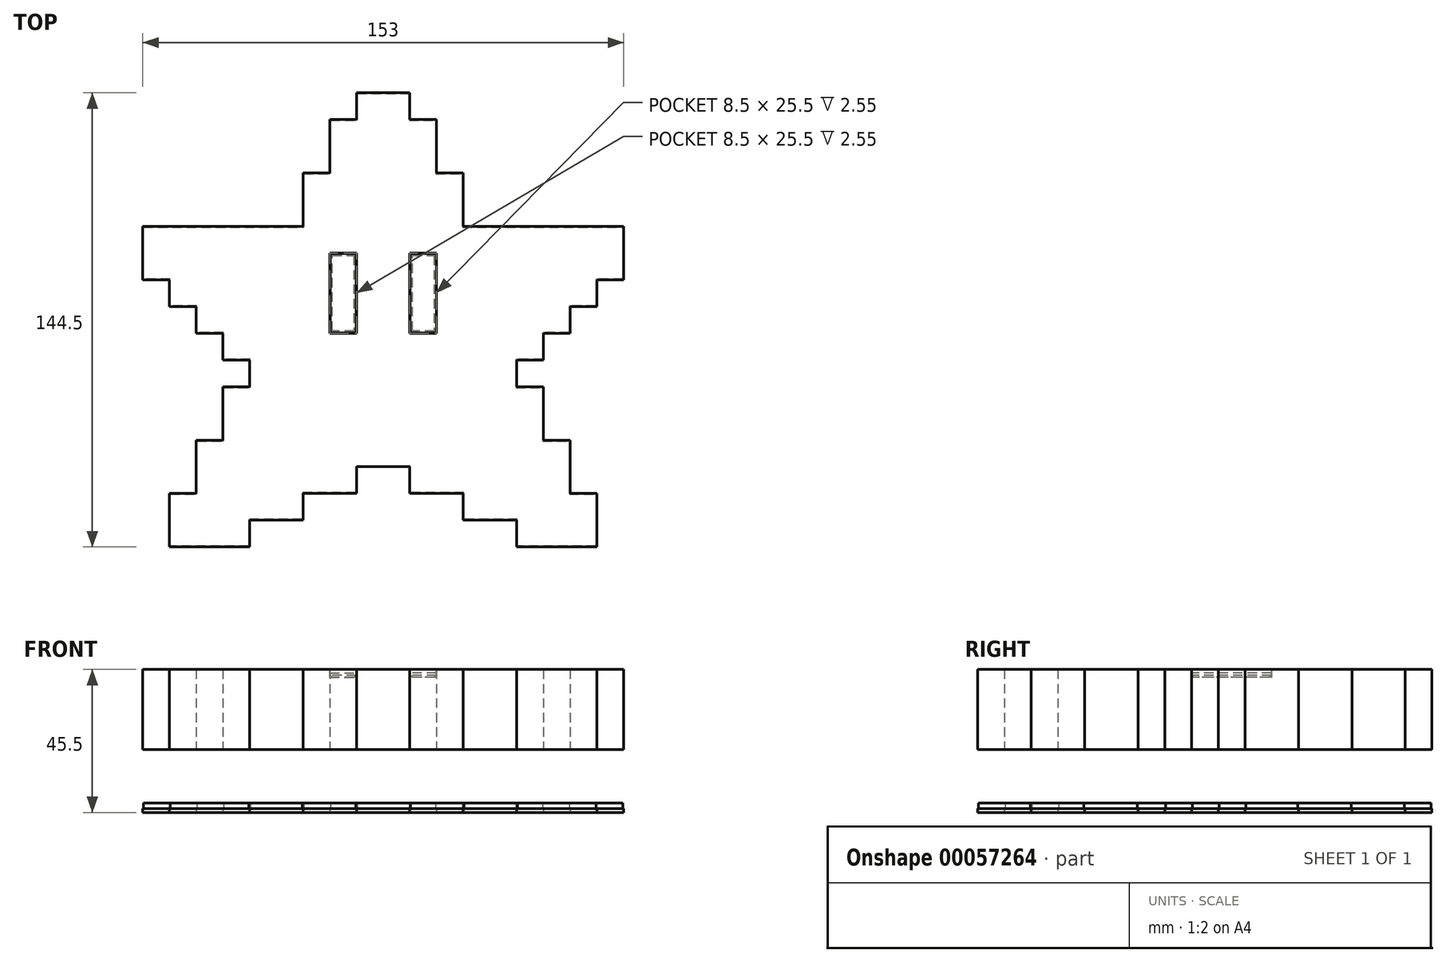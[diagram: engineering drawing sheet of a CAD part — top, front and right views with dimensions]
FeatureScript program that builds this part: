
annotation { "Feature Type Name" : "Feature", "Feature Type Description" : "" }
export const myFeature = defineFeature(function(context is Context, id is Id, definition is map)
    precondition{}
    {
        {
            assignVariable(context, id + "F0", {"name" : "pix", "anyValue" : 8.5});
        }
        {
            var Q0;
            Q0=qCreatedBy(makeId("Top.planeOp"),FACE);
            var sketch = newSketch(context, id + "F1", { "sketchPlane" : qUnion([Q0])});
            skLineSegment(sketch, "E0", {"start": v(0, 85) * mm, "end": v(-8.5, 85) * mm});
            skLineSegment(sketch, "E1", {"start": v(-8.5, 85) * mm, "end": v(-8.5, 76.5) * mm});
            skLineSegment(sketch, "E2", {"start": v(-8.5, 76.5) * mm, "end": v(-17, 76.5) * mm});
            skLineSegment(sketch, "E3", {"start": v(-17, 76.5) * mm, "end": v(-17, 59.5) * mm});
            skLineSegment(sketch, "E4", {"start": v(-17, 59.5) * mm, "end": v(-25.5, 59.5) * mm});
            skLineSegment(sketch, "E5", {"start": v(-25.5, 59.5) * mm, "end": v(-25.5, 42.5) * mm});
            skLineSegment(sketch, "E6", {"start": v(-25.5, 42.5) * mm, "end": v(-76.5, 42.5) * mm});
            skLineSegment(sketch, "E7", {"start": v(-76.5, 42.5) * mm, "end": v(-76.5, 25.5) * mm});
            skLineSegment(sketch, "E8", {"start": v(-76.5, 25.5) * mm, "end": v(-68, 25.5) * mm});
            skLineSegment(sketch, "E9", {"start": v(-68, 25.5) * mm, "end": v(-68, 17) * mm});
            skLineSegment(sketch, "E10", {"start": v(-68, 17) * mm, "end": v(-59.5, 17) * mm});
            skLineSegment(sketch, "E11", {"start": v(-59.5, 17) * mm, "end": v(-59.5, 8.5) * mm});
            skLineSegment(sketch, "E12", {"start": v(-59.5, 8.5) * mm, "end": v(-51, 8.5) * mm});
            skLineSegment(sketch, "E13", {"start": v(-51, 8.5) * mm, "end": v(-51, 0) * mm});
            skLineSegment(sketch, "E14", {"start": v(-51, 0) * mm, "end": v(-42.5, 0) * mm});
            skLineSegment(sketch, "E15", {"start": v(-42.5, 0) * mm, "end": v(-42.5, -8.5) * mm});
            skLineSegment(sketch, "E16", {"start": v(-42.5, -8.5) * mm, "end": v(-51, -8.5) * mm});
            skLineSegment(sketch, "E17", {"start": v(-51, -8.5) * mm, "end": v(-51, -25.5) * mm});
            skLineSegment(sketch, "E18", {"start": v(-51, -25.5) * mm, "end": v(-59.5, -25.5) * mm});
            skLineSegment(sketch, "E19", {"start": v(-59.5, -25.5) * mm, "end": v(-59.5, -42.5) * mm});
            skLineSegment(sketch, "E20", {"start": v(-59.5, -42.5) * mm, "end": v(-68, -42.5) * mm});
            skLineSegment(sketch, "E21", {"start": v(-68, -42.5) * mm, "end": v(-68, -59.5) * mm});
            skLineSegment(sketch, "E22", {"start": v(-68, -59.5) * mm, "end": v(-42.5, -59.5) * mm});
            skLineSegment(sketch, "E23", {"start": v(-42.5, -59.5) * mm, "end": v(-42.5, -51) * mm});
            skLineSegment(sketch, "E24", {"start": v(-42.5, -51) * mm, "end": v(-25.5, -51) * mm});
            skLineSegment(sketch, "E25", {"start": v(-25.5, -51) * mm, "end": v(-25.5, -42.5) * mm});
            skLineSegment(sketch, "E26", {"start": v(-25.5, -42.5) * mm, "end": v(-8.5, -42.5) * mm});
            skLineSegment(sketch, "E27", {"start": v(-8.5, -42.5) * mm, "end": v(-8.5, -34) * mm});
            skLineSegment(sketch, "E28", {"start": v(-8.5, -34) * mm, "end": v(0, -34) * mm});
            skLineSegment(sketch, "E29.MirrorCS", {"start": v(42.5, -8.5) * mm, "end": v(51, -8.5) * mm});
            skLineSegment(sketch, "E30.MirrorCS", {"start": v(51, -25.5) * mm, "end": v(59.5, -25.5) * mm});
            skLineSegment(sketch, "E31.MirrorCS", {"start": v(25.5, 59.5) * mm, "end": v(25.5, 42.5) * mm});
            skLineSegment(sketch, "E32.MirrorCS", {"start": v(17, 59.5) * mm, "end": v(25.5, 59.5) * mm});
            skLineSegment(sketch, "E33.MirrorCS", {"start": v(25.5, 42.5) * mm, "end": v(76.5, 42.5) * mm});
            skLineSegment(sketch, "E34.MirrorCS", {"start": v(68, -59.5) * mm, "end": v(42.5, -59.5) * mm});
            skLineSegment(sketch, "E35.MirrorCS", {"start": v(59.5, -42.5) * mm, "end": v(68, -42.5) * mm});
            skLineSegment(sketch, "E36.MirrorCS", {"start": v(76.5, 42.5) * mm, "end": v(76.5, 25.5) * mm});
            skLineSegment(sketch, "E37.MirrorCS", {"start": v(42.5, -59.5) * mm, "end": v(42.5, -51) * mm});
            skLineSegment(sketch, "E38.MirrorCS", {"start": v(17, 76.5) * mm, "end": v(17, 59.5) * mm});
            skLineSegment(sketch, "E39.MirrorCS", {"start": v(76.5, 25.5) * mm, "end": v(68, 25.5) * mm});
            skLineSegment(sketch, "E40.MirrorCS", {"start": v(8.5, 76.5) * mm, "end": v(17, 76.5) * mm});
            skLineSegment(sketch, "E41.MirrorCS", {"start": v(8.5, -34) * mm, "end": v(0, -34) * mm});
            skLineSegment(sketch, "E42.MirrorCS", {"start": v(25.5, -42.5) * mm, "end": v(8.5, -42.5) * mm});
            skLineSegment(sketch, "E43.MirrorCS", {"start": v(68, 17) * mm, "end": v(59.5, 17) * mm});
            skLineSegment(sketch, "E44.MirrorCS", {"start": v(68, 25.5) * mm, "end": v(68, 17) * mm});
            skLineSegment(sketch, "E45.MirrorCS", {"start": v(25.5, -51) * mm, "end": v(25.5, -42.5) * mm});
            skLineSegment(sketch, "E46.MirrorCS", {"start": v(8.5, -42.5) * mm, "end": v(8.5, -34) * mm});
            skLineSegment(sketch, "E47.MirrorCS", {"start": v(42.5, -51) * mm, "end": v(25.5, -51) * mm});
            skLineSegment(sketch, "E48.MirrorCS", {"start": v(8.5, 85) * mm, "end": v(8.5, 76.5) * mm});
            skLineSegment(sketch, "E49.MirrorCS", {"start": v(68, -42.5) * mm, "end": v(68, -59.5) * mm});
            skLineSegment(sketch, "E50.MirrorCS", {"start": v(0, 85) * mm, "end": v(8.5, 85) * mm});
            skLineSegment(sketch, "E51.MirrorCS", {"start": v(59.5, 8.5) * mm, "end": v(51, 8.5) * mm});
            skLineSegment(sketch, "E52.MirrorCS", {"start": v(51, 0) * mm, "end": v(42.5, 0) * mm});
            skLineSegment(sketch, "E53.MirrorCS", {"start": v(59.5, -25.5) * mm, "end": v(59.5, -42.5) * mm});
            skLineSegment(sketch, "E54.MirrorCS", {"start": v(51, 8.5) * mm, "end": v(51, 0) * mm});
            skLineSegment(sketch, "E55.MirrorCS", {"start": v(59.5, 17) * mm, "end": v(59.5, 8.5) * mm});
            skLineSegment(sketch, "E56.MirrorCS", {"start": v(51, -8.5) * mm, "end": v(51, -25.5) * mm});
            skLineSegment(sketch, "E57.MirrorCS", {"start": v(42.5, 0) * mm, "end": v(42.5, -8.5) * mm});
            skSolve(sketch);
        }
        {
            var Q0;
            Q0=makeQuery(id+"F1.imprint","IMPRINT",FACE,{"disambiguationData":[TD([[makeQuery(id+"F1.imprint","IMPRINT",EDGE,{"derivedFrom":sQuery(id+"F1.wireOp",EDGE,"E0")}),1.0]])]});
            extrude(context, id + "F2", {"entities" : qUnion([Q0]), "depth" : (3 * getVariable(context, 'pix')) * mm});
        }
        {
            var Q0;
            Q0=makeQuery(id+"F2.opExtrude","CAP_FACE",FACE,{"disambiguationData":[OSD([sQuery(id+"F1.wireOp",EDGE,"E0"),sQuery(id+"F1.wireOp",EDGE,"E1"),sQuery(id+"F1.wireOp",EDGE,"E2"),sQuery(id+"F1.wireOp",EDGE,"E3"),sQuery(id+"F1.wireOp",EDGE,"E4"),sQuery(id+"F1.wireOp",EDGE,"E5"),sQuery(id+"F1.wireOp",EDGE,"E6"),sQuery(id+"F1.wireOp",EDGE,"E7"),sQuery(id+"F1.wireOp",EDGE,"E8"),sQuery(id+"F1.wireOp",EDGE,"E9"),sQuery(id+"F1.wireOp",EDGE,"E10"),sQuery(id+"F1.wireOp",EDGE,"E11"),sQuery(id+"F1.wireOp",EDGE,"E12"),sQuery(id+"F1.wireOp",EDGE,"E13"),sQuery(id+"F1.wireOp",EDGE,"E14"),sQuery(id+"F1.wireOp",EDGE,"E15"),sQuery(id+"F1.wireOp",EDGE,"E16"),sQuery(id+"F1.wireOp",EDGE,"E17"),sQuery(id+"F1.wireOp",EDGE,"E18"),sQuery(id+"F1.wireOp",EDGE,"E19"),sQuery(id+"F1.wireOp",EDGE,"E20"),sQuery(id+"F1.wireOp",EDGE,"E21"),sQuery(id+"F1.wireOp",EDGE,"E22"),sQuery(id+"F1.wireOp",EDGE,"E23"),sQuery(id+"F1.wireOp",EDGE,"E24"),sQuery(id+"F1.wireOp",EDGE,"E25"),sQuery(id+"F1.wireOp",EDGE,"E26"),sQuery(id+"F1.wireOp",EDGE,"E27"),sQuery(id+"F1.wireOp",EDGE,"E28"),sQuery(id+"F1.wireOp",EDGE,"E29.MirrorCS"),sQuery(id+"F1.wireOp",EDGE,"E30.MirrorCS"),sQuery(id+"F1.wireOp",EDGE,"E31.MirrorCS"),sQuery(id+"F1.wireOp",EDGE,"E32.MirrorCS"),sQuery(id+"F1.wireOp",EDGE,"E33.MirrorCS"),sQuery(id+"F1.wireOp",EDGE,"E34.MirrorCS"),sQuery(id+"F1.wireOp",EDGE,"E35.MirrorCS"),sQuery(id+"F1.wireOp",EDGE,"E36.MirrorCS"),sQuery(id+"F1.wireOp",EDGE,"E37.MirrorCS"),sQuery(id+"F1.wireOp",EDGE,"E38.MirrorCS"),sQuery(id+"F1.wireOp",EDGE,"E39.MirrorCS"),sQuery(id+"F1.wireOp",EDGE,"E40.MirrorCS"),sQuery(id+"F1.wireOp",EDGE,"E41.MirrorCS"),sQuery(id+"F1.wireOp",EDGE,"E42.MirrorCS"),sQuery(id+"F1.wireOp",EDGE,"E43.MirrorCS"),sQuery(id+"F1.wireOp",EDGE,"E44.MirrorCS"),sQuery(id+"F1.wireOp",EDGE,"E45.MirrorCS"),sQuery(id+"F1.wireOp",EDGE,"E46.MirrorCS"),sQuery(id+"F1.wireOp",EDGE,"E47.MirrorCS"),sQuery(id+"F1.wireOp",EDGE,"E48.MirrorCS"),sQuery(id+"F1.wireOp",EDGE,"E49.MirrorCS"),sQuery(id+"F1.wireOp",EDGE,"E50.MirrorCS"),sQuery(id+"F1.wireOp",EDGE,"E51.MirrorCS"),sQuery(id+"F1.wireOp",EDGE,"E52.MirrorCS"),sQuery(id+"F1.wireOp",EDGE,"E53.MirrorCS"),sQuery(id+"F1.wireOp",EDGE,"E54.MirrorCS"),sQuery(id+"F1.wireOp",EDGE,"E55.MirrorCS"),sQuery(id+"F1.wireOp",EDGE,"E56.MirrorCS"),sQuery(id+"F1.wireOp",EDGE,"E57.MirrorCS")])],"isStart":false});
            var sketch = newSketch(context, id + "F3", { "sketchPlane" : qUnion([Q0])});
            skPoint(sketch, "E58.0", {"position": v(-17, 59.5) * mm});
            skLineSegment(sketch, "E59.bottom", {"start": v(-17, 34) * mm, "end": v(-8.5, 34) * mm});
            skLineSegment(sketch, "E59.top", {"start": v(-17, 8.5) * mm, "end": v(-8.5, 8.5) * mm});
            skLineSegment(sketch, "E59.left", {"start": v(-17, 34) * mm, "end": v(-17, 8.5) * mm});
            skLineSegment(sketch, "E59.right", {"start": v(-8.5, 34) * mm, "end": v(-8.5, 8.5) * mm});
            skLineSegment(sketch, "E60.MirrorCS", {"start": v(8.5, 34) * mm, "end": v(8.5, 8.5) * mm});
            skLineSegment(sketch, "E61.MirrorCS", {"start": v(17, 34) * mm, "end": v(17, 8.5) * mm});
            skLineSegment(sketch, "E62.MirrorCS", {"start": v(17, 8.5) * mm, "end": v(8.5, 8.5) * mm});
            skLineSegment(sketch, "E63.MirrorCS", {"start": v(17, 34) * mm, "end": v(8.5, 34) * mm});
            skPoint(sketch, "E64.MirrorP", {"position": v(17, 59.5) * mm});
            skSolve(sketch);
        }
        {
            var Q0;
            Q0=makeQuery(id+"F3.imprint","IMPRINT",FACE,{"disambiguationData":[TD([[makeQuery(id+"F3.imprint","IMPRINT",EDGE,{"derivedFrom":sQuery(id+"F3.wireOp",EDGE,"E59.bottom")}),-1.0]])]});
            var Q1;
            Q1=makeQuery(id+"F3.imprint","IMPRINT",FACE,{"disambiguationData":[TD([[makeQuery(id+"F3.imprint","IMPRINT",EDGE,{"derivedFrom":sQuery(id+"F3.wireOp",EDGE,"E60.MirrorCS")}),1.0]])]});
            extrude(context, id + "F4", {"entities" : qUnion([Q0, Q1]), "operationType" : NewBodyOperationType.REMOVE, "oppositeDirection" : true, "depth" : 0.3 * (getVariable(context, 'pix')) * mm});
        }
        {
            var Q0;
            Q0=makeQuery(id+"F2.opExtrude","CAP_FACE",FACE,{"disambiguationData":[OSD([sQuery(id+"F1.wireOp",EDGE,"E0"),sQuery(id+"F1.wireOp",EDGE,"E1"),sQuery(id+"F1.wireOp",EDGE,"E2"),sQuery(id+"F1.wireOp",EDGE,"E3"),sQuery(id+"F1.wireOp",EDGE,"E4"),sQuery(id+"F1.wireOp",EDGE,"E5"),sQuery(id+"F1.wireOp",EDGE,"E6"),sQuery(id+"F1.wireOp",EDGE,"E7"),sQuery(id+"F1.wireOp",EDGE,"E8"),sQuery(id+"F1.wireOp",EDGE,"E9"),sQuery(id+"F1.wireOp",EDGE,"E10"),sQuery(id+"F1.wireOp",EDGE,"E11"),sQuery(id+"F1.wireOp",EDGE,"E12"),sQuery(id+"F1.wireOp",EDGE,"E13"),sQuery(id+"F1.wireOp",EDGE,"E14"),sQuery(id+"F1.wireOp",EDGE,"E15"),sQuery(id+"F1.wireOp",EDGE,"E16"),sQuery(id+"F1.wireOp",EDGE,"E17"),sQuery(id+"F1.wireOp",EDGE,"E18"),sQuery(id+"F1.wireOp",EDGE,"E19"),sQuery(id+"F1.wireOp",EDGE,"E20"),sQuery(id+"F1.wireOp",EDGE,"E21"),sQuery(id+"F1.wireOp",EDGE,"E22"),sQuery(id+"F1.wireOp",EDGE,"E23"),sQuery(id+"F1.wireOp",EDGE,"E24"),sQuery(id+"F1.wireOp",EDGE,"E25"),sQuery(id+"F1.wireOp",EDGE,"E26"),sQuery(id+"F1.wireOp",EDGE,"E27"),sQuery(id+"F1.wireOp",EDGE,"E28"),sQuery(id+"F1.wireOp",EDGE,"E29.MirrorCS"),sQuery(id+"F1.wireOp",EDGE,"E30.MirrorCS"),sQuery(id+"F1.wireOp",EDGE,"E31.MirrorCS"),sQuery(id+"F1.wireOp",EDGE,"E32.MirrorCS"),sQuery(id+"F1.wireOp",EDGE,"E33.MirrorCS"),sQuery(id+"F1.wireOp",EDGE,"E34.MirrorCS"),sQuery(id+"F1.wireOp",EDGE,"E35.MirrorCS"),sQuery(id+"F1.wireOp",EDGE,"E36.MirrorCS"),sQuery(id+"F1.wireOp",EDGE,"E37.MirrorCS"),sQuery(id+"F1.wireOp",EDGE,"E38.MirrorCS"),sQuery(id+"F1.wireOp",EDGE,"E39.MirrorCS"),sQuery(id+"F1.wireOp",EDGE,"E40.MirrorCS"),sQuery(id+"F1.wireOp",EDGE,"E41.MirrorCS"),sQuery(id+"F1.wireOp",EDGE,"E42.MirrorCS"),sQuery(id+"F1.wireOp",EDGE,"E43.MirrorCS"),sQuery(id+"F1.wireOp",EDGE,"E44.MirrorCS"),sQuery(id+"F1.wireOp",EDGE,"E45.MirrorCS"),sQuery(id+"F1.wireOp",EDGE,"E46.MirrorCS"),sQuery(id+"F1.wireOp",EDGE,"E47.MirrorCS"),sQuery(id+"F1.wireOp",EDGE,"E48.MirrorCS"),sQuery(id+"F1.wireOp",EDGE,"E49.MirrorCS"),sQuery(id+"F1.wireOp",EDGE,"E50.MirrorCS"),sQuery(id+"F1.wireOp",EDGE,"E51.MirrorCS"),sQuery(id+"F1.wireOp",EDGE,"E52.MirrorCS"),sQuery(id+"F1.wireOp",EDGE,"E53.MirrorCS"),sQuery(id+"F1.wireOp",EDGE,"E54.MirrorCS"),sQuery(id+"F1.wireOp",EDGE,"E55.MirrorCS"),sQuery(id+"F1.wireOp",EDGE,"E56.MirrorCS"),sQuery(id+"F1.wireOp",EDGE,"E57.MirrorCS")])],"isStart":false});
            var sketch = newSketch(context, id + "F5", { "sketchPlane" : qUnion([Q0])});
            skPoint(sketch, "E65", {"position": v(0, 76.5) * mm});
            skLineSegment(sketch, "E66.rect.bottom", {"start": v(-2.13, 76.5) * mm, "end": v(2.12, 76.5) * mm});
            skLineSegment(sketch, "E66.rect.top", {"start": v(-2.13, 72.25) * mm, "end": v(2.12, 72.25) * mm});
            skLineSegment(sketch, "E66.rect.left", {"start": v(-2.13, 76.5) * mm, "end": v(-2.13, 72.25) * mm});
            skLineSegment(sketch, "E66.rect.right", {"start": v(2.12, 76.5) * mm, "end": v(2.12, 72.25) * mm});
            skPoint(sketch, "E66.rect.middle", {"position": v(0, 74.38) * mm});
            skSolve(sketch);
        }
        {
            var Q0;
            Q0=makeQuery(id+"F4.boolean.opBoolean","COPY",FACE,{"derivedFrom":makeQuery(id+"F4.opExtrude","CAP_FACE",FACE,{"disambiguationData":[OSD([sQuery(id+"F3.wireOp",EDGE,"E59.bottom"),sQuery(id+"F3.wireOp",EDGE,"E59.top"),sQuery(id+"F3.wireOp",EDGE,"E59.left"),sQuery(id+"F3.wireOp",EDGE,"E59.right")])],"isStart":false})});
            var sketch = newSketch(context, id + "F6", { "sketchPlane" : qUnion([Q0])});
            skLineSegment(sketch, "E67.0", {"start": v(-16.9, 33.9) * mm, "end": v(-8.6, 33.9) * mm});
            skLineSegment(sketch, "E67.1", {"start": v(-16.9, 33.9) * mm, "end": v(-16.9, 8.6) * mm});
            skLineSegment(sketch, "E67.2", {"start": v(-16.9, 8.6) * mm, "end": v(-8.6, 8.6) * mm});
            skLineSegment(sketch, "E67.3", {"start": v(-8.6, 33.9) * mm, "end": v(-8.6, 8.6) * mm});
            skLineSegment(sketch, "E68.MirrorCS", {"start": v(16.9, 33.9) * mm, "end": v(8.6, 33.9) * mm});
            skLineSegment(sketch, "E69.MirrorCS", {"start": v(16.9, 8.6) * mm, "end": v(8.6, 8.6) * mm});
            skLineSegment(sketch, "E70.MirrorCS", {"start": v(8.6, 33.9) * mm, "end": v(8.6, 8.6) * mm});
            skLineSegment(sketch, "E71.MirrorCS", {"start": v(16.9, 33.9) * mm, "end": v(16.9, 8.6) * mm});
            skSolve(sketch);
        }
        {
            var Q0;
            Q0=makeQuery(id+"F6.imprint","IMPRINT",FACE,{"disambiguationData":[TD([[makeQuery(id+"F6.imprint","IMPRINT",EDGE,{"derivedFrom":sQuery(id+"F6.wireOp",EDGE,"E67.0")}),-1.0]])]});
            var Q1;
            Q1=makeQuery(id+"F6.imprint","IMPRINT",FACE,{"disambiguationData":[TD([[makeQuery(id+"F6.imprint","IMPRINT",EDGE,{"derivedFrom":sQuery(id+"F6.wireOp",EDGE,"E68.MirrorCS")}),1.0]])]});
            extrude(context, id + "F7", {"entities" : qUnion([Q0, Q1]), "depth" : 1.5 * mm});
        }
        {
            var Q0;
            Q0=makeQuery(id+"F7.opExtrude","CAP_FACE",FACE,{"disambiguationData":[OSD([sQuery(id+"F6.wireOp",EDGE,"E67.0"),sQuery(id+"F6.wireOp",EDGE,"E67.1"),sQuery(id+"F6.wireOp",EDGE,"E67.2"),sQuery(id+"F6.wireOp",EDGE,"E67.3")])],"isStart":true});
            var Q1;
            Q1=makeQuery(id+"F7.opExtrude","CAP_FACE",FACE,{"disambiguationData":[OSD([sQuery(id+"F6.wireOp",EDGE,"E68.MirrorCS"),sQuery(id+"F6.wireOp",EDGE,"E69.MirrorCS"),sQuery(id+"F6.wireOp",EDGE,"E70.MirrorCS"),sQuery(id+"F6.wireOp",EDGE,"E71.MirrorCS")])],"isStart":true});
            chamfer(context, id + "F8", {"entities" : qUnion([Q0, Q1]), "width" : 0.7 * mm, "tangentPropagation" : true});
        }
        {
            var Q0;
            Q0=makeQuery(id+"F2.opExtrude","CAP_FACE",FACE,{"disambiguationData":[OSD([sQuery(id+"F1.wireOp",EDGE,"E0"),sQuery(id+"F1.wireOp",EDGE,"E1"),sQuery(id+"F1.wireOp",EDGE,"E2"),sQuery(id+"F1.wireOp",EDGE,"E3"),sQuery(id+"F1.wireOp",EDGE,"E4"),sQuery(id+"F1.wireOp",EDGE,"E5"),sQuery(id+"F1.wireOp",EDGE,"E6"),sQuery(id+"F1.wireOp",EDGE,"E7"),sQuery(id+"F1.wireOp",EDGE,"E8"),sQuery(id+"F1.wireOp",EDGE,"E9"),sQuery(id+"F1.wireOp",EDGE,"E10"),sQuery(id+"F1.wireOp",EDGE,"E11"),sQuery(id+"F1.wireOp",EDGE,"E12"),sQuery(id+"F1.wireOp",EDGE,"E13"),sQuery(id+"F1.wireOp",EDGE,"E14"),sQuery(id+"F1.wireOp",EDGE,"E15"),sQuery(id+"F1.wireOp",EDGE,"E16"),sQuery(id+"F1.wireOp",EDGE,"E17"),sQuery(id+"F1.wireOp",EDGE,"E18"),sQuery(id+"F1.wireOp",EDGE,"E19"),sQuery(id+"F1.wireOp",EDGE,"E20"),sQuery(id+"F1.wireOp",EDGE,"E21"),sQuery(id+"F1.wireOp",EDGE,"E22"),sQuery(id+"F1.wireOp",EDGE,"E23"),sQuery(id+"F1.wireOp",EDGE,"E24"),sQuery(id+"F1.wireOp",EDGE,"E25"),sQuery(id+"F1.wireOp",EDGE,"E26"),sQuery(id+"F1.wireOp",EDGE,"E27"),sQuery(id+"F1.wireOp",EDGE,"E28"),sQuery(id+"F1.wireOp",EDGE,"E29.MirrorCS"),sQuery(id+"F1.wireOp",EDGE,"E30.MirrorCS"),sQuery(id+"F1.wireOp",EDGE,"E31.MirrorCS"),sQuery(id+"F1.wireOp",EDGE,"E32.MirrorCS"),sQuery(id+"F1.wireOp",EDGE,"E33.MirrorCS"),sQuery(id+"F1.wireOp",EDGE,"E34.MirrorCS"),sQuery(id+"F1.wireOp",EDGE,"E35.MirrorCS"),sQuery(id+"F1.wireOp",EDGE,"E36.MirrorCS"),sQuery(id+"F1.wireOp",EDGE,"E37.MirrorCS"),sQuery(id+"F1.wireOp",EDGE,"E38.MirrorCS"),sQuery(id+"F1.wireOp",EDGE,"E39.MirrorCS"),sQuery(id+"F1.wireOp",EDGE,"E40.MirrorCS"),sQuery(id+"F1.wireOp",EDGE,"E41.MirrorCS"),sQuery(id+"F1.wireOp",EDGE,"E42.MirrorCS"),sQuery(id+"F1.wireOp",EDGE,"E43.MirrorCS"),sQuery(id+"F1.wireOp",EDGE,"E44.MirrorCS"),sQuery(id+"F1.wireOp",EDGE,"E45.MirrorCS"),sQuery(id+"F1.wireOp",EDGE,"E46.MirrorCS"),sQuery(id+"F1.wireOp",EDGE,"E47.MirrorCS"),sQuery(id+"F1.wireOp",EDGE,"E48.MirrorCS"),sQuery(id+"F1.wireOp",EDGE,"E49.MirrorCS"),sQuery(id+"F1.wireOp",EDGE,"E50.MirrorCS"),sQuery(id+"F1.wireOp",EDGE,"E51.MirrorCS"),sQuery(id+"F1.wireOp",EDGE,"E52.MirrorCS"),sQuery(id+"F1.wireOp",EDGE,"E53.MirrorCS"),sQuery(id+"F1.wireOp",EDGE,"E54.MirrorCS"),sQuery(id+"F1.wireOp",EDGE,"E55.MirrorCS"),sQuery(id+"F1.wireOp",EDGE,"E56.MirrorCS"),sQuery(id+"F1.wireOp",EDGE,"E57.MirrorCS")])],"isStart":true});
            cPlane(context, id + "F9", {"entities" : qUnion([Q0]), "cplaneType" : CPlaneType.OFFSET, "offset" : 20 * mm, "width" : 150 * mm, "height" : 150 * mm});
        }
        {
            var Q0;
            Q0=qCreatedBy(id+"F9.planeOp",FACE);
            var sketch = newSketch(context, id + "F10", { "sketchPlane" : qUnion([Q0])});
            skLineSegment(sketch, "E72.0.0", {"start": v(-8.5, -85) * mm, "end": v(8.5, -85) * mm});
            skLineSegment(sketch, "E72.0.1", {"start": v(8.5, -85) * mm, "end": v(8.5, -76.5) * mm});
            skLineSegment(sketch, "E72.0.2", {"start": v(8.5, -76.5) * mm, "end": v(17, -76.5) * mm});
            skLineSegment(sketch, "E72.0.3", {"start": v(17, -76.5) * mm, "end": v(17, -59.5) * mm});
            skLineSegment(sketch, "E72.0.4", {"start": v(17, -59.5) * mm, "end": v(25.5, -59.5) * mm});
            skLineSegment(sketch, "E72.0.5", {"start": v(25.5, -59.5) * mm, "end": v(25.5, -42.5) * mm});
            skLineSegment(sketch, "E72.0.6", {"start": v(25.5, -42.5) * mm, "end": v(76.5, -42.5) * mm});
            skLineSegment(sketch, "E72.0.7", {"start": v(76.5, -42.5) * mm, "end": v(76.5, -25.5) * mm});
            skLineSegment(sketch, "E72.0.8", {"start": v(76.5, -25.5) * mm, "end": v(68, -25.5) * mm});
            skLineSegment(sketch, "E72.0.9", {"start": v(68, -25.5) * mm, "end": v(68, -17) * mm});
            skLineSegment(sketch, "E72.0.10", {"start": v(68, -17) * mm, "end": v(59.5, -17) * mm});
            skLineSegment(sketch, "E72.0.11", {"start": v(59.5, -17) * mm, "end": v(59.5, -8.5) * mm});
            skLineSegment(sketch, "E72.0.12", {"start": v(59.5, -8.5) * mm, "end": v(51, -8.5) * mm});
            skLineSegment(sketch, "E72.0.13", {"start": v(51, -8.5) * mm, "end": v(51, 0) * mm});
            skLineSegment(sketch, "E72.0.14", {"start": v(51, 0) * mm, "end": v(42.5, 0) * mm});
            skLineSegment(sketch, "E72.0.15", {"start": v(42.5, 0) * mm, "end": v(42.5, 8.5) * mm});
            skLineSegment(sketch, "E72.0.16", {"start": v(42.5, 8.5) * mm, "end": v(51, 8.5) * mm});
            skLineSegment(sketch, "E72.0.17", {"start": v(51, 8.5) * mm, "end": v(51, 25.5) * mm});
            skLineSegment(sketch, "E72.0.18", {"start": v(51, 25.5) * mm, "end": v(59.5, 25.5) * mm});
            skLineSegment(sketch, "E72.0.19", {"start": v(59.5, 25.5) * mm, "end": v(59.5, 42.5) * mm});
            skLineSegment(sketch, "E72.0.20", {"start": v(59.5, 42.5) * mm, "end": v(68, 42.5) * mm});
            skLineSegment(sketch, "E72.0.21", {"start": v(68, 42.5) * mm, "end": v(68, 59.5) * mm});
            skLineSegment(sketch, "E72.0.22", {"start": v(68, 59.5) * mm, "end": v(42.5, 59.5) * mm});
            skLineSegment(sketch, "E72.0.23", {"start": v(42.5, 59.5) * mm, "end": v(42.5, 51) * mm});
            skLineSegment(sketch, "E72.0.24", {"start": v(42.5, 51) * mm, "end": v(25.5, 51) * mm});
            skLineSegment(sketch, "E72.0.25", {"start": v(25.5, 51) * mm, "end": v(25.5, 42.5) * mm});
            skLineSegment(sketch, "E72.0.26", {"start": v(25.5, 42.5) * mm, "end": v(8.5, 42.5) * mm});
            skLineSegment(sketch, "E72.0.27", {"start": v(8.5, 42.5) * mm, "end": v(8.5, 34) * mm});
            skLineSegment(sketch, "E72.0.28", {"start": v(8.5, 34) * mm, "end": v(-8.5, 34) * mm});
            skLineSegment(sketch, "E72.0.29", {"start": v(-8.5, 34) * mm, "end": v(-8.5, 42.5) * mm});
            skLineSegment(sketch, "E72.0.30", {"start": v(-8.5, 42.5) * mm, "end": v(-25.5, 42.5) * mm});
            skLineSegment(sketch, "E72.0.31", {"start": v(-25.5, 42.5) * mm, "end": v(-25.5, 51) * mm});
            skLineSegment(sketch, "E72.0.32", {"start": v(-25.5, 51) * mm, "end": v(-42.5, 51) * mm});
            skLineSegment(sketch, "E72.0.33", {"start": v(-42.5, 51) * mm, "end": v(-42.5, 59.5) * mm});
            skLineSegment(sketch, "E72.0.34", {"start": v(-42.5, 59.5) * mm, "end": v(-68, 59.5) * mm});
            skLineSegment(sketch, "E72.0.35", {"start": v(-68, 59.5) * mm, "end": v(-68, 42.5) * mm});
            skLineSegment(sketch, "E72.0.36", {"start": v(-68, 42.5) * mm, "end": v(-59.5, 42.5) * mm});
            skLineSegment(sketch, "E72.0.37", {"start": v(-59.5, 42.5) * mm, "end": v(-59.5, 25.5) * mm});
            skLineSegment(sketch, "E72.0.38", {"start": v(-59.5, 25.5) * mm, "end": v(-51, 25.5) * mm});
            skLineSegment(sketch, "E72.0.39", {"start": v(-51, 25.5) * mm, "end": v(-51, 8.5) * mm});
            skLineSegment(sketch, "E72.0.40", {"start": v(-51, 8.5) * mm, "end": v(-42.5, 8.5) * mm});
            skLineSegment(sketch, "E72.0.41", {"start": v(-42.5, 8.5) * mm, "end": v(-42.5, 0) * mm});
            skLineSegment(sketch, "E72.0.42", {"start": v(-42.5, 0) * mm, "end": v(-51, 0) * mm});
            skLineSegment(sketch, "E72.0.43", {"start": v(-51, 0) * mm, "end": v(-51, -8.5) * mm});
            skLineSegment(sketch, "E72.0.44", {"start": v(-51, -8.5) * mm, "end": v(-59.5, -8.5) * mm});
            skLineSegment(sketch, "E72.0.45", {"start": v(-59.5, -8.5) * mm, "end": v(-59.5, -17) * mm});
            skLineSegment(sketch, "E72.0.46", {"start": v(-59.5, -17) * mm, "end": v(-68, -17) * mm});
            skLineSegment(sketch, "E72.0.47", {"start": v(-68, -17) * mm, "end": v(-68, -25.5) * mm});
            skLineSegment(sketch, "E72.0.48", {"start": v(-68, -25.5) * mm, "end": v(-76.5, -25.5) * mm});
            skLineSegment(sketch, "E72.0.49", {"start": v(-76.5, -25.5) * mm, "end": v(-76.5, -42.5) * mm});
            skLineSegment(sketch, "E72.0.50", {"start": v(-76.5, -42.5) * mm, "end": v(-25.5, -42.5) * mm});
            skLineSegment(sketch, "E72.0.51", {"start": v(-25.5, -42.5) * mm, "end": v(-25.5, -59.5) * mm});
            skLineSegment(sketch, "E72.0.52", {"start": v(-25.5, -59.5) * mm, "end": v(-17, -59.5) * mm});
            skLineSegment(sketch, "E72.0.53", {"start": v(-17, -59.5) * mm, "end": v(-17, -76.5) * mm});
            skLineSegment(sketch, "E72.0.54", {"start": v(-17, -76.5) * mm, "end": v(-8.5, -76.5) * mm});
            skLineSegment(sketch, "E72.0.55", {"start": v(-8.5, -76.5) * mm, "end": v(-8.5, -85) * mm});
            skLineSegment(sketch, "E73.0", {"start": v(-42.75, 59.25) * mm, "end": v(-67.75, 59.25) * mm});
            skLineSegment(sketch, "E73.1", {"start": v(-42.75, 50.75) * mm, "end": v(-42.75, 59.25) * mm});
            skLineSegment(sketch, "E73.2", {"start": v(-25.75, 50.75) * mm, "end": v(-42.75, 50.75) * mm});
            skLineSegment(sketch, "E73.3", {"start": v(-25.75, 42.25) * mm, "end": v(-25.75, 50.75) * mm});
            skLineSegment(sketch, "E73.4", {"start": v(-8.75, 42.25) * mm, "end": v(-25.75, 42.25) * mm});
            skLineSegment(sketch, "E73.5", {"start": v(-8.75, 33.75) * mm, "end": v(-8.75, 42.25) * mm});
            skLineSegment(sketch, "E73.6", {"start": v(8.75, 33.75) * mm, "end": v(-8.75, 33.75) * mm});
            skLineSegment(sketch, "E73.7", {"start": v(8.75, 42.25) * mm, "end": v(8.75, 33.75) * mm});
            skLineSegment(sketch, "E73.8", {"start": v(25.75, 42.25) * mm, "end": v(8.75, 42.25) * mm});
            skLineSegment(sketch, "E73.9", {"start": v(25.75, 50.75) * mm, "end": v(25.75, 42.25) * mm});
            skLineSegment(sketch, "E73.10", {"start": v(-8.25, -84.75) * mm, "end": v(8.25, -84.75) * mm});
            skLineSegment(sketch, "E73.11", {"start": v(-8.25, -76.25) * mm, "end": v(-8.25, -84.75) * mm});
            skLineSegment(sketch, "E73.12", {"start": v(-16.75, -76.25) * mm, "end": v(-8.25, -76.25) * mm});
            skLineSegment(sketch, "E73.13", {"start": v(-16.75, -59.25) * mm, "end": v(-16.75, -76.25) * mm});
            skLineSegment(sketch, "E73.14", {"start": v(-25.25, -59.25) * mm, "end": v(-16.75, -59.25) * mm});
            skLineSegment(sketch, "E73.15", {"start": v(-25.25, -42.25) * mm, "end": v(-25.25, -59.25) * mm});
            skLineSegment(sketch, "E73.16", {"start": v(-76.25, -42.25) * mm, "end": v(-25.25, -42.25) * mm});
            skLineSegment(sketch, "E73.17", {"start": v(-76.25, -25.75) * mm, "end": v(-76.25, -42.25) * mm});
            skLineSegment(sketch, "E73.18", {"start": v(-67.75, -25.75) * mm, "end": v(-76.25, -25.75) * mm});
            skLineSegment(sketch, "E73.19", {"start": v(-67.75, -17.25) * mm, "end": v(-67.75, -25.75) * mm});
            skLineSegment(sketch, "E73.20", {"start": v(-59.25, -17.25) * mm, "end": v(-67.75, -17.25) * mm});
            skLineSegment(sketch, "E73.21", {"start": v(-59.25, -8.75) * mm, "end": v(-59.25, -17.25) * mm});
            skLineSegment(sketch, "E73.22", {"start": v(-59.25, 25.75) * mm, "end": v(-50.75, 25.75) * mm});
            skLineSegment(sketch, "E73.23", {"start": v(-59.25, 42.75) * mm, "end": v(-59.25, 25.75) * mm});
            skLineSegment(sketch, "E73.24", {"start": v(-67.75, 42.75) * mm, "end": v(-59.25, 42.75) * mm});
            skLineSegment(sketch, "E73.25", {"start": v(-67.75, 59.25) * mm, "end": v(-67.75, 42.75) * mm});
            skLineSegment(sketch, "E73.26", {"start": v(-50.75, 25.75) * mm, "end": v(-50.75, 8.75) * mm});
            skLineSegment(sketch, "E73.27", {"start": v(-50.75, 8.75) * mm, "end": v(-42.25, 8.75) * mm});
            skLineSegment(sketch, "E73.28", {"start": v(-42.25, 8.75) * mm, "end": v(-42.25, -0.25) * mm});
            skLineSegment(sketch, "E73.29", {"start": v(-42.25, -0.25) * mm, "end": v(-50.75, -0.25) * mm});
            skLineSegment(sketch, "E73.30", {"start": v(-50.75, -0.25) * mm, "end": v(-50.75, -8.75) * mm});
            skLineSegment(sketch, "E73.31", {"start": v(-50.75, -8.75) * mm, "end": v(-59.25, -8.75) * mm});
            skLineSegment(sketch, "E73.32", {"start": v(8.25, -84.75) * mm, "end": v(8.25, -76.25) * mm});
            skLineSegment(sketch, "E73.33", {"start": v(8.25, -76.25) * mm, "end": v(16.75, -76.25) * mm});
            skLineSegment(sketch, "E73.34", {"start": v(16.75, -76.25) * mm, "end": v(16.75, -59.25) * mm});
            skLineSegment(sketch, "E73.35", {"start": v(16.75, -59.25) * mm, "end": v(25.25, -59.25) * mm});
            skLineSegment(sketch, "E73.36", {"start": v(25.25, -59.25) * mm, "end": v(25.25, -42.25) * mm});
            skLineSegment(sketch, "E73.37", {"start": v(25.25, -42.25) * mm, "end": v(76.25, -42.25) * mm});
            skLineSegment(sketch, "E73.38", {"start": v(76.25, -42.25) * mm, "end": v(76.25, -25.75) * mm});
            skLineSegment(sketch, "E73.39", {"start": v(76.25, -25.75) * mm, "end": v(67.75, -25.75) * mm});
            skLineSegment(sketch, "E73.40", {"start": v(67.75, -25.75) * mm, "end": v(67.75, -17.25) * mm});
            skLineSegment(sketch, "E73.41", {"start": v(67.75, -17.25) * mm, "end": v(59.25, -17.25) * mm});
            skLineSegment(sketch, "E73.42", {"start": v(59.25, -17.25) * mm, "end": v(59.25, -8.75) * mm});
            skLineSegment(sketch, "E73.43", {"start": v(59.25, -8.75) * mm, "end": v(50.75, -8.75) * mm});
            skLineSegment(sketch, "E73.44", {"start": v(50.75, -8.75) * mm, "end": v(50.75, -0.25) * mm});
            skLineSegment(sketch, "E73.45", {"start": v(50.75, -0.25) * mm, "end": v(42.25, -0.25) * mm});
            skLineSegment(sketch, "E73.46", {"start": v(42.25, -0.25) * mm, "end": v(42.25, 8.75) * mm});
            skLineSegment(sketch, "E73.47", {"start": v(42.25, 8.75) * mm, "end": v(50.75, 8.75) * mm});
            skLineSegment(sketch, "E73.48", {"start": v(50.75, 8.75) * mm, "end": v(50.75, 25.75) * mm});
            skLineSegment(sketch, "E73.49", {"start": v(50.75, 25.75) * mm, "end": v(59.25, 25.75) * mm});
            skLineSegment(sketch, "E73.50", {"start": v(59.25, 25.75) * mm, "end": v(59.25, 42.75) * mm});
            skLineSegment(sketch, "E73.51", {"start": v(59.25, 42.75) * mm, "end": v(67.75, 42.75) * mm});
            skLineSegment(sketch, "E73.52", {"start": v(67.75, 42.75) * mm, "end": v(67.75, 59.25) * mm});
            skLineSegment(sketch, "E73.53", {"start": v(67.75, 59.25) * mm, "end": v(42.75, 59.25) * mm});
            skLineSegment(sketch, "E73.54", {"start": v(42.75, 59.25) * mm, "end": v(42.75, 50.75) * mm});
            skLineSegment(sketch, "E73.55", {"start": v(42.75, 50.75) * mm, "end": v(25.75, 50.75) * mm});
            skSolve(sketch);
        }
        {
            var Q0;
            Q0=makeQuery(id+"F10.imprint","IMPRINT",FACE,{"disambiguationData":[TD([[makeQuery(id+"F10.imprint","IMPRINT",EDGE,{"derivedFrom":sQuery(id+"F10.wireOp",EDGE,"E73.0")}),1.0]])]});
            extrude(context, id + "F11", {"entities" : qUnion([Q0]), "oppositeDirection" : true, "depth" : 3 * mm});
        }
        {
            var Q0;
            Q0=makeQuery(id+"F10.imprint","IMPRINT",FACE,{"disambiguationData":[TD([[makeQuery(id+"F10.imprint","IMPRINT",EDGE,{"derivedFrom":sQuery(id+"F10.wireOp",EDGE,"E72.0.0")}),1.0]])]});
            extrude(context, id + "F12", {"entities" : qUnion([Q0]), "operationType" : NewBodyOperationType.ADD, "oppositeDirection" : true, "depth" : 1.2 * mm});
        }
    });
